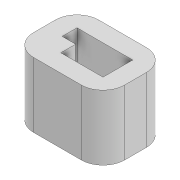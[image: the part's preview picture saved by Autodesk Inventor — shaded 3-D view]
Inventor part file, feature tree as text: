
AUTODESK INVENTOR PART (.ipt)
format: ipt  version: 2021 (Build 250183000, 183)  size: 155,648 bytes
history: native  units: mm
features: extrude x2, sketch x2, fillet x1, chamfer x1
ambient origin geometry x8: Origin, YZ Plane, XZ Plane, XY Plane, X Axis, Y Axis, Z Axis, Center Point
bodies: Volumenkörper1 (feature_tree)
feature tree (6):
  extrude  "Extrusion1"  Depth=12.0mm
  fillet  "Rundung1"  Radius=5.5mm
  extrude  "Extrusion3"  Depth=2.75mm
  chamfer  "Fase2"  Distance=7.8mm
  sketch  "Skizze1"  dims[d0=16.8mm d1=12.0mm d2=5.5mm]
  sketch  "Skizze3"  dims[d3=10.3mm d4=2.75mm d5=7.8mm d6=2.75mm d7=3.25mm d8=3.25mm d9=12.0mm d10=0.0mm d18=4.0mm d21=3.9mm d22=21.554816mm d23=3.9mm d24=21.554816mm d25=7.8mm d26=9.86111mm d27=1.55mm d28=1.55mm d29=1.55mm d30=180.0deg d31=21.554816mm d32=1.55mm d33=3.9mm d34=21.554816mm d35=1.55mm d36=0.0mm d37=1.35mm d38=1.35mm d39=7.35mm d42=3.7mm d43=0.0mm d50=4.725mm d51=4.725mm d52=2.747845mm d53=2.747845mm d54=0.5mm d55=0.0mm d56=0.5mm d57=2.0mm d58=45.0deg]
